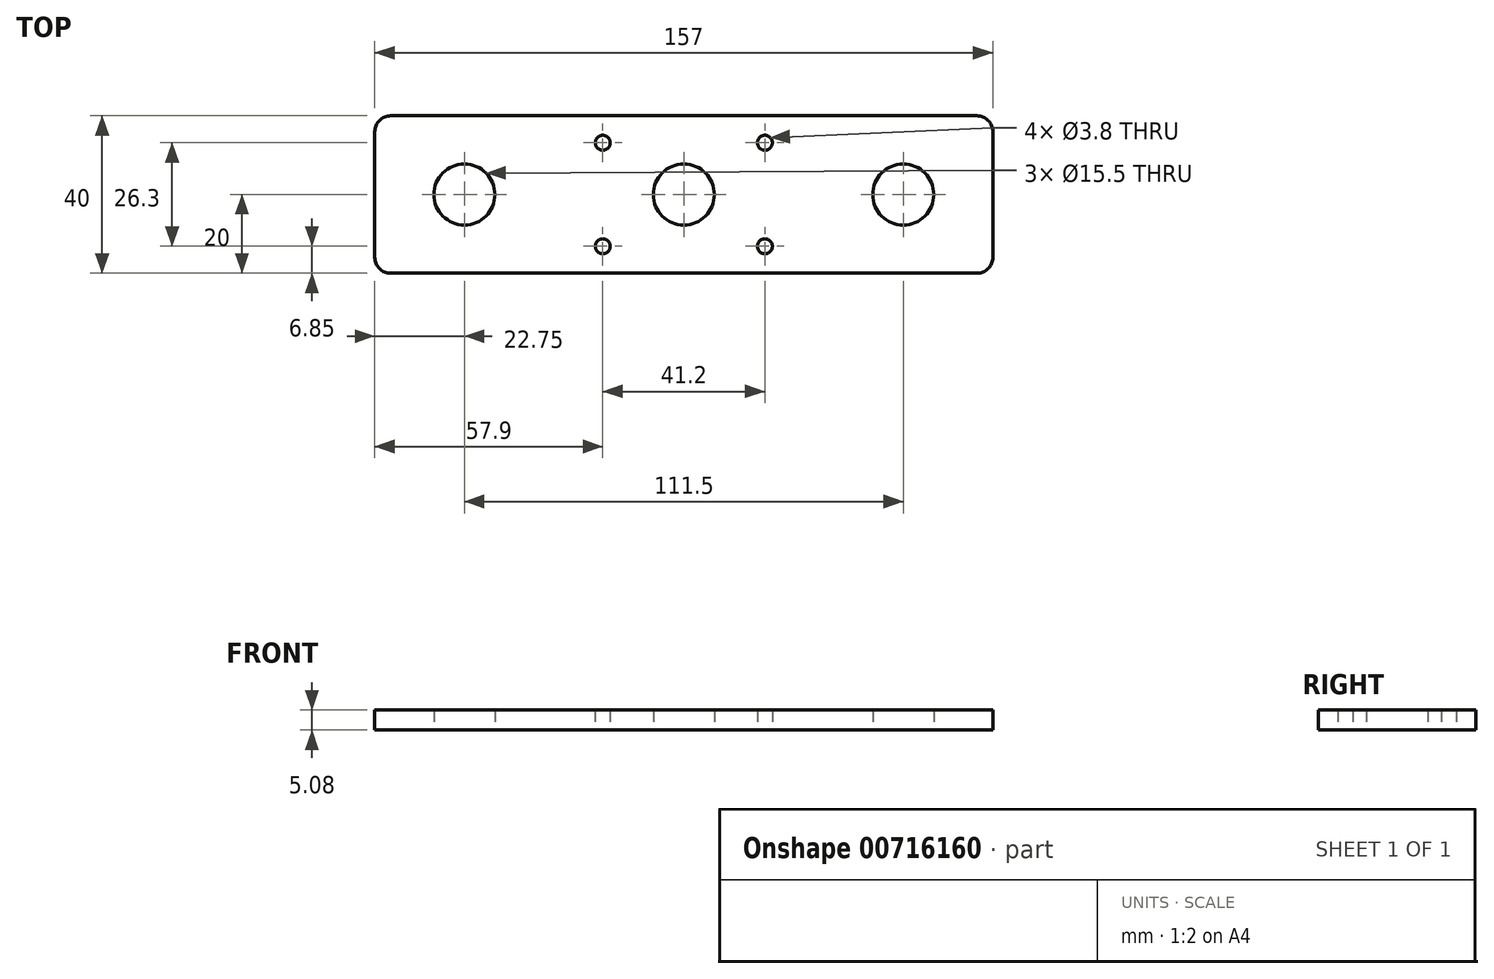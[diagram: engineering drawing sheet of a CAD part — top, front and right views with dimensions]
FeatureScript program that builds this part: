
annotation { "Feature Type Name" : "Feature", "Feature Type Description" : "" }
export const myFeature = defineFeature(function(context is Context, id is Id, definition is map)
    precondition{}
    {
        {
            var Q0;
            Q0=qCreatedBy(makeId("Top.planeOp"),FACE);
            var sketch = newSketch(context, id + "F0", { "sketchPlane" : qUnion([Q0])});
            skLineSegment(sketch, "E0.bottom", {"start": v(4, 0) * mm, "end": v(153, 0) * mm});
            skLineSegment(sketch, "E0.top", {"start": v(4, 40) * mm, "end": v(153, 40) * mm});
            skLineSegment(sketch, "E0.left", {"start": v(0, 4) * mm, "end": v(0, 36) * mm});
            skLineSegment(sketch, "E0.right", {"start": v(157, 4) * mm, "end": v(157, 36) * mm});
            skLineSegment(sketch, "E1", {"start": v(0, 20) * mm, "end": v(157, 20) * mm, "construction": true});
            skLineSegment(sketch, "E2", {"start": v(78.5, 40) * mm, "end": v(78.5, 0) * mm, "construction": true});
            skCircle(sketch, "E3", {"center": v(78.5, 20) * mm, "radius": 7.75 * mm});
            skCircle(sketch, "E4", {"center": v(22.75, 20) * mm, "radius": 7.75 * mm});
            skCircle(sketch, "E5", {"center": v(57.9, 33.15) * mm, "radius": 1.9 * mm});
            skCircle(sketch, "E6.MirrorC", {"center": v(99.1, 33.15) * mm, "radius": 1.9 * mm});
            skCircle(sketch, "E7.MirrorC", {"center": v(134.25, 20) * mm, "radius": 7.75 * mm});
            skCircle(sketch, "E8.MirrorC", {"center": v(57.9, 6.85) * mm, "radius": 1.9 * mm});
            skCircle(sketch, "E9.MirrorC", {"center": v(99.1, 6.85) * mm, "radius": 1.9 * mm});
            skPoint(sketch, "E10.visualSharp", {"position": v(0, 40) * mm});
            skArc(sketch, "E10.filletArc", {"start": v(4, 40) * mm, "mid": v(1.17, 38.83) * mm, "end": v(0, 36) * mm});
            skPoint(sketch, "E11.visualSharp", {"position": v(157, 40) * mm});
            skArc(sketch, "E11.filletArc", {"start": v(157, 36) * mm, "mid": v(155.83, 38.83) * mm, "end": v(153, 40) * mm});
            skPoint(sketch, "E12.visualSharp", {"position": v(157, 0) * mm});
            skArc(sketch, "E12.filletArc", {"start": v(153, 0) * mm, "mid": v(155.83, 1.17) * mm, "end": v(157, 4) * mm});
            skPoint(sketch, "E13.visualSharp", {"position": v(0, 0) * mm});
            skArc(sketch, "E13.filletArc", {"start": v(0, 4) * mm, "mid": v(1.17, 1.17) * mm, "end": v(4, 0) * mm});
            skSolve(sketch);
        }
        {
            var Q0;
            Q0=makeQuery(id+"F0.imprint","IMPRINT",FACE,{"disambiguationData":[TD([[makeQuery(id+"F0.imprint","IMPRINT",EDGE,{"derivedFrom":sQuery(id+"F0.wireOp",EDGE,"E0.bottom")}),1.0]])]});
            extrude(context, id + "F1", {"entities" : qUnion([Q0]), "depth" : 5.08 * mm, "offsetDistance" : 25 * mm});
        }
    });
